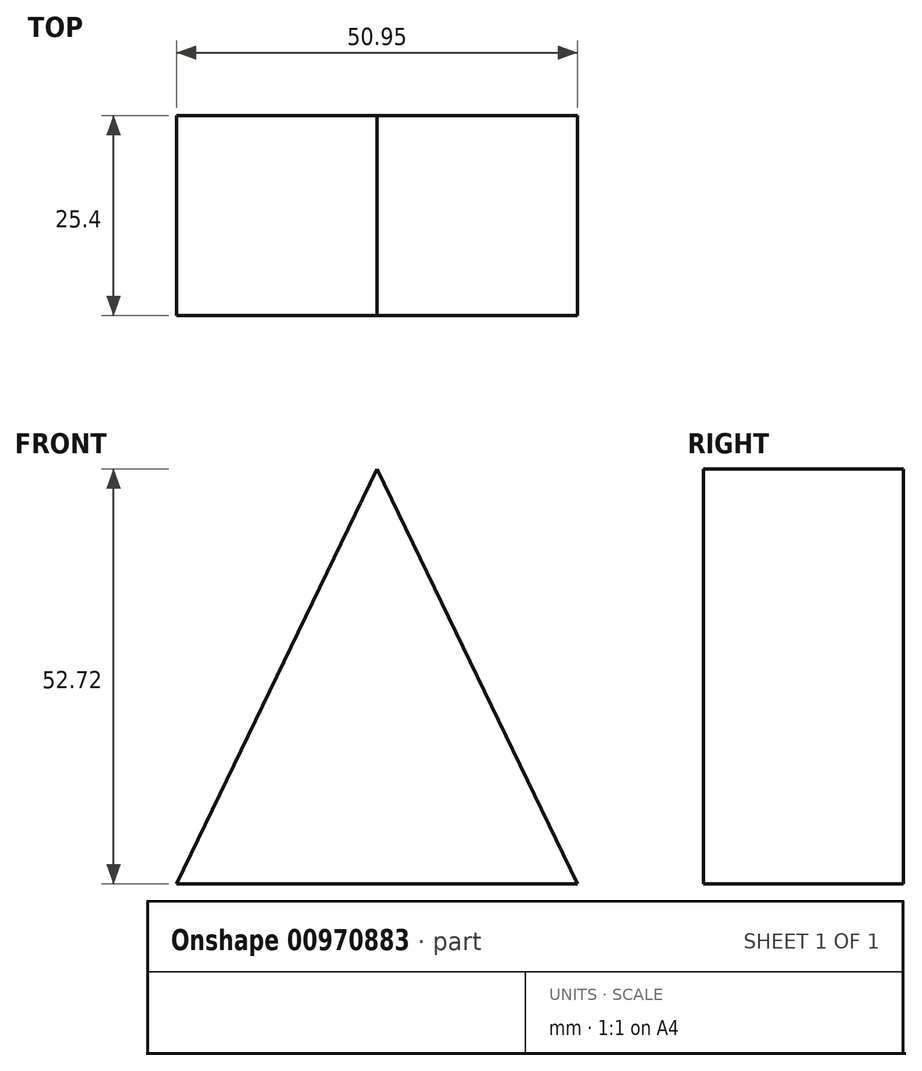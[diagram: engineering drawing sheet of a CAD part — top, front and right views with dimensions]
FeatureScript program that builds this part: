
annotation { "Feature Type Name" : "Feature", "Feature Type Description" : "" }
export const myFeature = defineFeature(function(context is Context, id is Id, definition is map)
    precondition{}
    {
        {
            var Q0;
            Q0=qCreatedBy(makeId("Front.planeOp"),FACE);
            var sketch = newSketch(context, id + "F0", { "sketchPlane" : qUnion([Q0])});
            skLineSegment(sketch, "E0", {"start": v(-50.95, -30.84) * mm, "end": v(0, -30.84) * mm});
            skLineSegment(sketch, "E1", {"start": v(-25.48, -30.84) * mm, "end": v(-25.48, 21.88) * mm});
            skLineSegment(sketch, "E2", {"start": v(-25.48, 21.88) * mm, "end": v(-50.95, -30.84) * mm});
            skLineSegment(sketch, "E3", {"start": v(-25.48, 21.88) * mm, "end": v(0, -30.84) * mm});
            skSolve(sketch);
        }
        {
            var Q0;
            Q0 = qSketchRegion(id + "F0", true);
            extrude(context, id + "F1", {"entities" : qUnion([Q0]), "depth" : 25.4 * mm, "offsetDistance" : 25.4 * mm});
        }
    });
